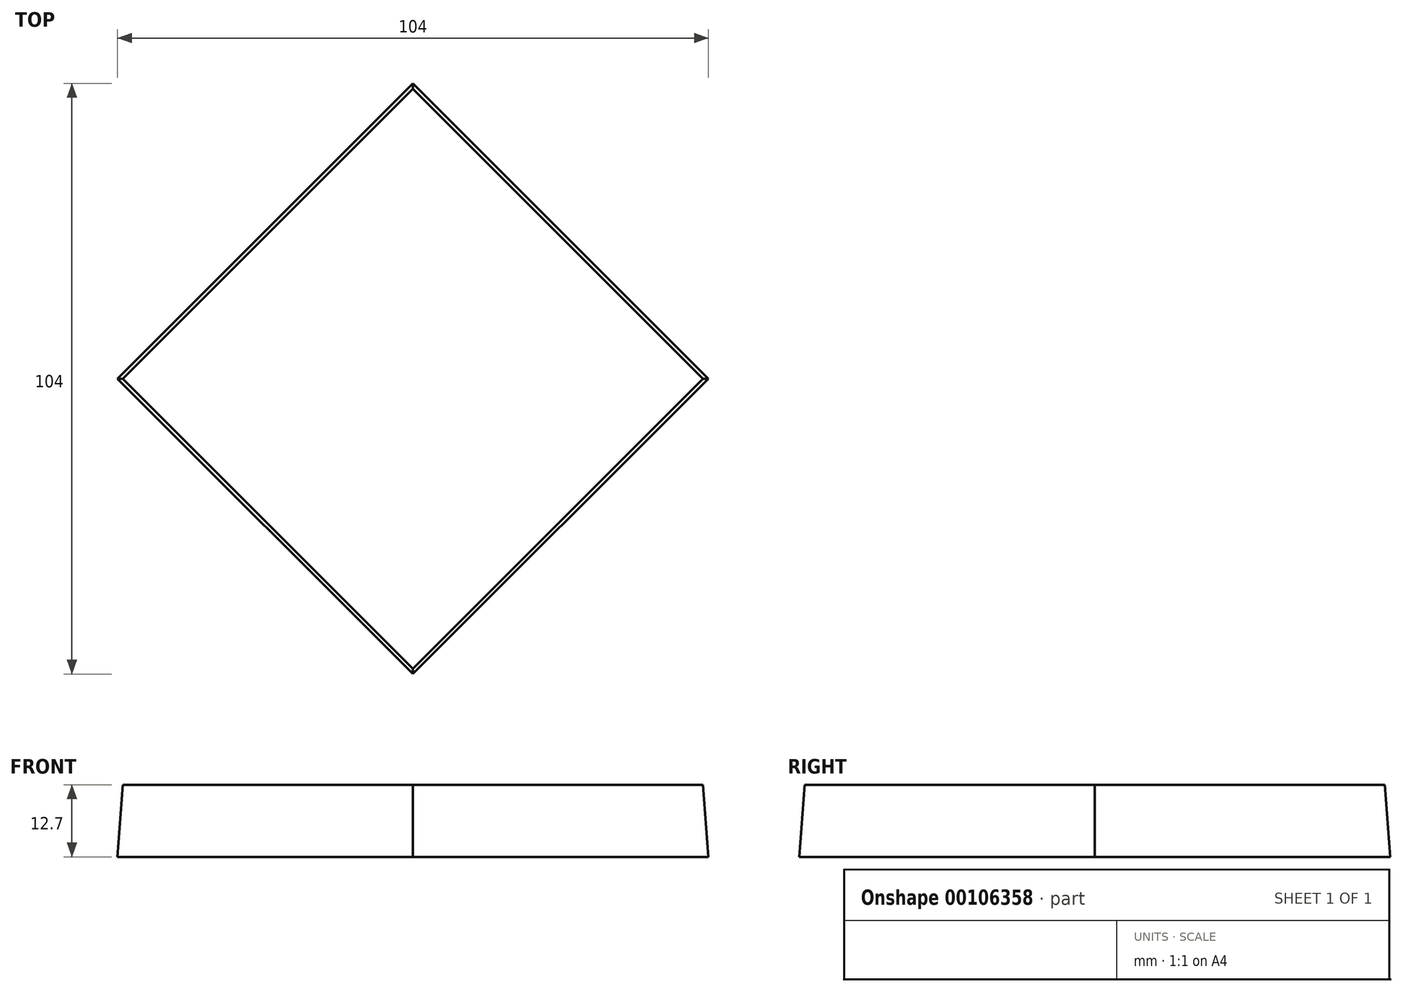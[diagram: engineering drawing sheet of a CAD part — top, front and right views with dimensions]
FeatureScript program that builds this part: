
annotation { "Feature Type Name" : "Feature", "Feature Type Description" : "" }
export const myFeature = defineFeature(function(context is Context, id is Id, definition is map)
    precondition{}
    {
        {
            var Q0;
            Q0=qCreatedBy(makeId("Top.planeOp"),FACE);
            var sketch = newSketch(context, id + "F0", { "sketchPlane" : qUnion([Q0])});
            skLineSegment(sketch, "E0.bottom", {"start": v(36.77, -36.77) * mm, "end": v(-36.77, -36.77) * mm});
            skLineSegment(sketch, "E0.top", {"start": v(36.77, 36.77) * mm, "end": v(-36.77, 36.77) * mm});
            skLineSegment(sketch, "E0.left", {"start": v(36.77, -36.77) * mm, "end": v(36.77, 36.77) * mm});
            skLineSegment(sketch, "E0.right", {"start": v(-36.77, -36.77) * mm, "end": v(-36.77, 36.77) * mm});
            skPoint(sketch, "E0.middle", {"position": v(0, 0) * mm});
            skSolve(sketch);
        }
        {
            var Q0;
            Q0 = qSketchRegion(id + "F0", true);
            extrude(context, id + "F1", {"entities" : qUnion([Q0]), "depth" : 12.7 * mm, "hasDraft" : true, "draftAngle" : 3 * degree, "draftPullDirection" : true});
        }
        {
            var Q0;
            Q0=qCreatedBy(makeId("Front.planeOp"),FACE);
            var sketch = newSketch(context, id + "F2", { "sketchPlane" : qUnion([Q0])});
            skLineSegment(sketch, "E1", {"start": v(0, 0) * mm, "end": v(0, 73.61) * mm});
            skSolve(sketch);
        }
        {
            var Q0;
            Q0=makeQuery(id+"F1.opExtrude","SWEPT_BODY",BODY,{"disambiguationData":[OSD([sQuery(id+"F0.wireOp",EDGE,"E0.bottom"),sQuery(id+"F0.wireOp",EDGE,"E0.top"),sQuery(id+"F0.wireOp",EDGE,"E0.left"),sQuery(id+"F0.wireOp",EDGE,"E0.right")])]});
            var Q1;
            Q1=sQuery(id+"F2.wireOp",EDGE,"E1");
            transform(context, id + "F3", {"entities" : qUnion([Q0]), "transformType" : TransformType.ROTATION, "transformAxis" : qUnion([Q1]), "angle" : 45 * degree, "makeCopy" : false});
        }
    });
